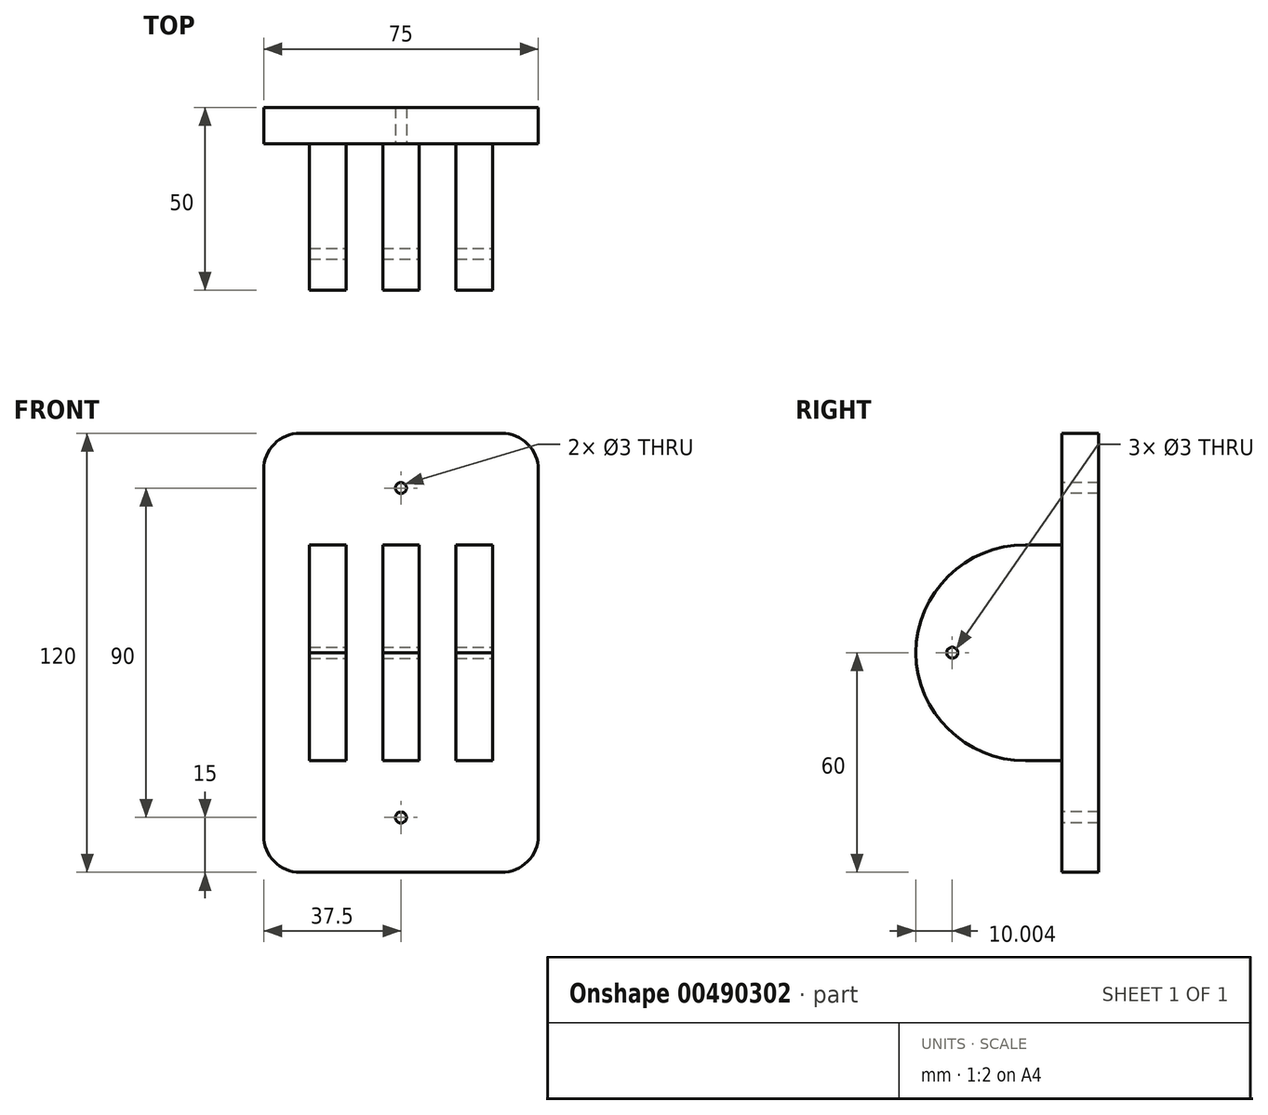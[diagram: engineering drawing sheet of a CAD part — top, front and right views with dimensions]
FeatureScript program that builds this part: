
annotation { "Feature Type Name" : "Feature", "Feature Type Description" : "" }
export const myFeature = defineFeature(function(context is Context, id is Id, definition is map)
    precondition{}
    {
        {
            var Q0;
            Q0=qCreatedBy(makeId("Front.planeOp"),FACE);
            var sketch = newSketch(context, id + "F0", { "sketchPlane" : qUnion([Q0])});
            skLineSegment(sketch, "E0.bottom", {"start": v(37.5, -60) * mm, "end": v(-37.5, -60) * mm});
            skLineSegment(sketch, "E0.top", {"start": v(37.5, 60) * mm, "end": v(-37.5, 60) * mm});
            skLineSegment(sketch, "E0.left", {"start": v(37.5, -60) * mm, "end": v(37.5, 60) * mm});
            skLineSegment(sketch, "E0.right", {"start": v(-37.5, -60) * mm, "end": v(-37.5, 60) * mm});
            skPoint(sketch, "E0.middle", {"position": v(0, 0) * mm});
            skSolve(sketch);
        }
        {
            var Q0;
            Q0 = qSketchRegion(id + "F0", true);
            extrude(context, id + "F1", {"entities" : qUnion([Q0]), "depth" : 10 * mm, "offsetDistance" : 25 * mm});
        }
        {
            var Q0;
            Q0=makeQuery(id+"F1.opExtrude","CAP_FACE",FACE,{"disambiguationData":[OSD([sQuery(id+"F0.wireOp",EDGE,"E0.bottom"),sQuery(id+"F0.wireOp",EDGE,"E0.top"),sQuery(id+"F0.wireOp",EDGE,"E0.left"),sQuery(id+"F0.wireOp",EDGE,"E0.right")])],"isStart":false});
            var sketch = newSketch(context, id + "F2", { "sketchPlane" : qUnion([Q0])});
            skCircle(sketch, "E1", {"center": v(0, -45) * mm, "radius": 1.5 * mm});
            skCircle(sketch, "E2", {"center": v(0, 45) * mm, "radius": 1.5 * mm});
            skPoint(sketch, "E2.centerSnap0", {"position": v(0, 60) * mm});
            skSolve(sketch);
        }
        {
            var Q0;
            Q0 = qSketchRegion(id + "F2", true);
            extrude(context, id + "F3", {"entities" : qUnion([Q0]), "operationType" : NewBodyOperationType.REMOVE, "oppositeDirection" : true, "depth" : 41.3 * mm, "offsetDistance" : 25 * mm});
        }
        {
            var Q0;
            Q0=makeQuery(id+"F1.opExtrude","CAP_FACE",FACE,{"disambiguationData":[OSD([sQuery(id+"F0.wireOp",EDGE,"E0.bottom"),sQuery(id+"F0.wireOp",EDGE,"E0.top"),sQuery(id+"F0.wireOp",EDGE,"E0.left"),sQuery(id+"F0.wireOp",EDGE,"E0.right")])],"isStart":false});
            var sketch = newSketch(context, id + "F4", { "sketchPlane" : qUnion([Q0])});
            skLineSegment(sketch, "E3.bottom", {"start": v(37.5, -29.52) * mm, "end": v(-37.5, -29.52) * mm});
            skLineSegment(sketch, "E3.top", {"start": v(37.5, 29.52) * mm, "end": v(-37.5, 29.52) * mm});
            skLineSegment(sketch, "E3.left", {"start": v(37.5, -29.52) * mm, "end": v(37.5, 29.52) * mm});
            skLineSegment(sketch, "E3.right", {"start": v(-37.5, -29.52) * mm, "end": v(-37.5, 29.52) * mm});
            skPoint(sketch, "E3.middle", {"position": v(0, 0) * mm});
            skSolve(sketch);
        }
        {
            var Q0;
            Q0 = qSketchRegion(id + "F4", true);
            extrude(context, id + "F5", {"entities" : qUnion([Q0]), "operationType" : NewBodyOperationType.ADD, "depth" : 40 * mm, "offsetDistance" : 25 * mm});
        }
        {
            var Q0;
            Q0=makeQuery(id+"F5.opExtrude","CAP_FACE",FACE,{"disambiguationData":[OSD([sQuery(id+"F4.wireOp",EDGE,"E3.bottom"),sQuery(id+"F4.wireOp",EDGE,"E3.top"),sQuery(id+"F4.wireOp",EDGE,"E3.left"),sQuery(id+"F4.wireOp",EDGE,"E3.right")])],"isStart":false});
            var sketch = newSketch(context, id + "F6", { "sketchPlane" : qUnion([Q0])});
            skLineSegment(sketch, "E4.bottom", {"start": v(-37.5, 29.52) * mm, "end": v(37.5, 29.52) * mm});
            skLineSegment(sketch, "E4.top", {"start": v(-37.5, -29.52) * mm, "end": v(37.5, -29.52) * mm});
            skLineSegment(sketch, "E4.left", {"start": v(-37.5, 29.52) * mm, "end": v(-37.5, -29.52) * mm});
            skLineSegment(sketch, "E4.right", {"start": v(37.5, 29.52) * mm, "end": v(37.5, -29.52) * mm});
            skLineSegment(sketch, "E5.bottom", {"start": v(-25, 29.52) * mm, "end": v(-15, 29.52) * mm});
            skLineSegment(sketch, "E5.top", {"start": v(-25, -29.52) * mm, "end": v(-15, -29.52) * mm});
            skLineSegment(sketch, "E5.left", {"start": v(-25, 29.52) * mm, "end": v(-25, -29.52) * mm});
            skLineSegment(sketch, "E5.right", {"start": v(-15, 29.52) * mm, "end": v(-15, -29.52) * mm});
            skLineSegment(sketch, "E6.bottom", {"start": v(-5, 29.52) * mm, "end": v(5, 29.52) * mm});
            skLineSegment(sketch, "E6.top", {"start": v(-5, -29.52) * mm, "end": v(5, -29.52) * mm});
            skLineSegment(sketch, "E6.left", {"start": v(-5, 29.52) * mm, "end": v(-5, -29.52) * mm});
            skLineSegment(sketch, "E6.right", {"start": v(5, 29.52) * mm, "end": v(5, -29.52) * mm});
            skLineSegment(sketch, "E7.bottom", {"start": v(15, 29.52) * mm, "end": v(25, 29.52) * mm});
            skLineSegment(sketch, "E7.top", {"start": v(15, -29.52) * mm, "end": v(25, -29.52) * mm});
            skLineSegment(sketch, "E7.left", {"start": v(15, 29.52) * mm, "end": v(15, -29.52) * mm});
            skLineSegment(sketch, "E7.right", {"start": v(25, 29.52) * mm, "end": v(25, -29.52) * mm});
            skSolve(sketch);
        }
        {
            var Q0;
            Q0=makeQuery(id+"F1.opExtrude","SWEPT_EDGE",EDGE,{"disambiguationData":[OSD([sQuery(id+"F0.wireOp",EDGE,"E0.top"),sQuery(id+"F0.wireOp",EDGE,"E0.left")])]});
            var Q1;
            Q1=makeQuery(id+"F1.opExtrude","SWEPT_EDGE",EDGE,{"disambiguationData":[OSD([sQuery(id+"F0.wireOp",EDGE,"E0.top"),sQuery(id+"F0.wireOp",EDGE,"E0.right")])]});
            var Q2;
            Q2=makeQuery(id+"F1.opExtrude","SWEPT_EDGE",EDGE,{"disambiguationData":[OSD([sQuery(id+"F0.wireOp",EDGE,"E0.bottom"),sQuery(id+"F0.wireOp",EDGE,"E0.right")])]});
            var Q3;
            Q3=makeQuery(id+"F1.opExtrude","SWEPT_EDGE",EDGE,{"disambiguationData":[OSD([sQuery(id+"F0.wireOp",EDGE,"E0.bottom"),sQuery(id+"F0.wireOp",EDGE,"E0.left")])]});
            fillet(context, id + "F7", {"entities" : qUnion([Q0, Q1, Q2, Q3]), "radius" : 10 * mm, "tangentPropagation" : true, "allowEdgeOverflow" : false});
        }
        {
            var Q0;
            {var subQ0=sQuery(id+"F6.wireOp",EDGE,"E4.left");Q0=makeQuery(id+"F6.imprint","IMPRINT",FACE,{"disambiguationData":[TD([[makeQuery(id+"F6.imprint","IMPRINT",EDGE,{"derivedFrom":subQ0}),-1.0]])]});}
            var Q1;
            {var subQ0=sQuery(id+"F6.wireOp",EDGE,"E5.right");Q1=makeQuery(id+"F6.imprint","IMPRINT",FACE,{"disambiguationData":[TD([[makeQuery(id+"F6.imprint","IMPRINT",EDGE,{"derivedFrom":subQ0}),1.0]])]});}
            var Q2;
            {var subQ0=sQuery(id+"F6.wireOp",EDGE,"E6.right");Q2=makeQuery(id+"F6.imprint","IMPRINT",FACE,{"disambiguationData":[TD([[makeQuery(id+"F6.imprint","IMPRINT",EDGE,{"derivedFrom":subQ0}),1.0]])]});}
            var Q3;
            {var subQ0=sQuery(id+"F6.wireOp",EDGE,"E4.right");Q3=makeQuery(id+"F6.imprint","IMPRINT",FACE,{"disambiguationData":[TD([[makeQuery(id+"F6.imprint","IMPRINT",EDGE,{"derivedFrom":subQ0}),1.0]])]});}
            extrude(context, id + "F8", {"entities" : qUnion([Q0, Q1, Q2, Q3]), "operationType" : NewBodyOperationType.REMOVE, "oppositeDirection" : true, "depth" : 40 * mm, "offsetDistance" : 25 * mm});
        }
        {
            var Q0;
            {var subQ0=sQuery(id+"F4.wireOp",EDGE,"E3.top");Q0=makeQuery(id+"F8.boolean.opBoolean","SPLIT",EDGE,{"disambiguationData":[TD([makeQuery(id+"F8.opExtrude","SWEPT_FACE",FACE,{"disambiguationData":[OSD([sQuery(id+"F6.wireOp",EDGE,"E7.left")])]})])],"derivedFrom":makeQuery(id+"F5.opExtrude","CAP_EDGE",EDGE,{"disambiguationData":[OSD([subQ0])],"isStart":false})});}
            var Q1;
            {var subQ0=sQuery(id+"F4.wireOp",EDGE,"E3.top");Q1=makeQuery(id+"F8.boolean.opBoolean","SPLIT",EDGE,{"disambiguationData":[TD([makeQuery(id+"F8.opExtrude","SWEPT_FACE",FACE,{"disambiguationData":[OSD([sQuery(id+"F6.wireOp",EDGE,"E6.left")])]})])],"derivedFrom":makeQuery(id+"F5.opExtrude","CAP_EDGE",EDGE,{"disambiguationData":[OSD([subQ0])],"isStart":false})});}
            var Q2;
            {var subQ0=sQuery(id+"F4.wireOp",EDGE,"E3.top");Q2=makeQuery(id+"F8.boolean.opBoolean","SPLIT",EDGE,{"disambiguationData":[TD([makeQuery(id+"F8.opExtrude","SWEPT_FACE",FACE,{"disambiguationData":[OSD([sQuery(id+"F6.wireOp",EDGE,"E5.left")])]})])],"derivedFrom":makeQuery(id+"F5.opExtrude","CAP_EDGE",EDGE,{"disambiguationData":[OSD([subQ0])],"isStart":false})});}
            var Q3;
            {var subQ0=sQuery(id+"F4.wireOp",EDGE,"E3.bottom");Q3=makeQuery(id+"F8.boolean.opBoolean","SPLIT",EDGE,{"disambiguationData":[TD([makeQuery(id+"F8.opExtrude","SWEPT_FACE",FACE,{"disambiguationData":[OSD([sQuery(id+"F6.wireOp",EDGE,"E5.left")])]})])],"derivedFrom":makeQuery(id+"F5.opExtrude","CAP_EDGE",EDGE,{"disambiguationData":[OSD([subQ0])],"isStart":false})});}
            var Q4;
            {var subQ0=sQuery(id+"F4.wireOp",EDGE,"E3.bottom");Q4=makeQuery(id+"F8.boolean.opBoolean","SPLIT",EDGE,{"disambiguationData":[TD([makeQuery(id+"F8.opExtrude","SWEPT_FACE",FACE,{"disambiguationData":[OSD([sQuery(id+"F6.wireOp",EDGE,"E6.left")])]})])],"derivedFrom":makeQuery(id+"F5.opExtrude","CAP_EDGE",EDGE,{"disambiguationData":[OSD([subQ0])],"isStart":false})});}
            var Q5;
            {var subQ0=sQuery(id+"F4.wireOp",EDGE,"E3.bottom");Q5=makeQuery(id+"F8.boolean.opBoolean","SPLIT",EDGE,{"disambiguationData":[TD([makeQuery(id+"F8.opExtrude","SWEPT_FACE",FACE,{"disambiguationData":[OSD([sQuery(id+"F6.wireOp",EDGE,"E7.left")])]})])],"derivedFrom":makeQuery(id+"F5.opExtrude","CAP_EDGE",EDGE,{"disambiguationData":[OSD([subQ0])],"isStart":false})});}
            fillet(context, id + "F9", {"entities" : qUnion([Q0, Q1, Q2, Q3, Q4, Q5]), "radius" : 30 * mm, "tangentPropagation" : true, "allowEdgeOverflow" : false});
        }
        {
            var Q0;
            Q0=makeQuery(id+"F8.boolean.opBoolean","COPY",FACE,{"derivedFrom":makeQuery(id+"F8.opExtrude","SWEPT_FACE",FACE,{"disambiguationData":[OSD([sQuery(id+"F6.wireOp",EDGE,"E7.right")])]})});
            var sketch = newSketch(context, id + "F10", { "sketchPlane" : qUnion([Q0])});
            skCircle(sketch, "E8", {"center": v(-40, 0) * mm, "radius": 1.5 * mm});
            skSolve(sketch);
        }
        {
            var Q0;
            Q0 = qSketchRegion(id + "F10", true);
            extrude(context, id + "F11", {"entities" : qUnion([Q0]), "operationType" : NewBodyOperationType.REMOVE, "oppositeDirection" : true, "depth" : 57.1 * mm, "offsetDistance" : 25 * mm});
        }
    });
